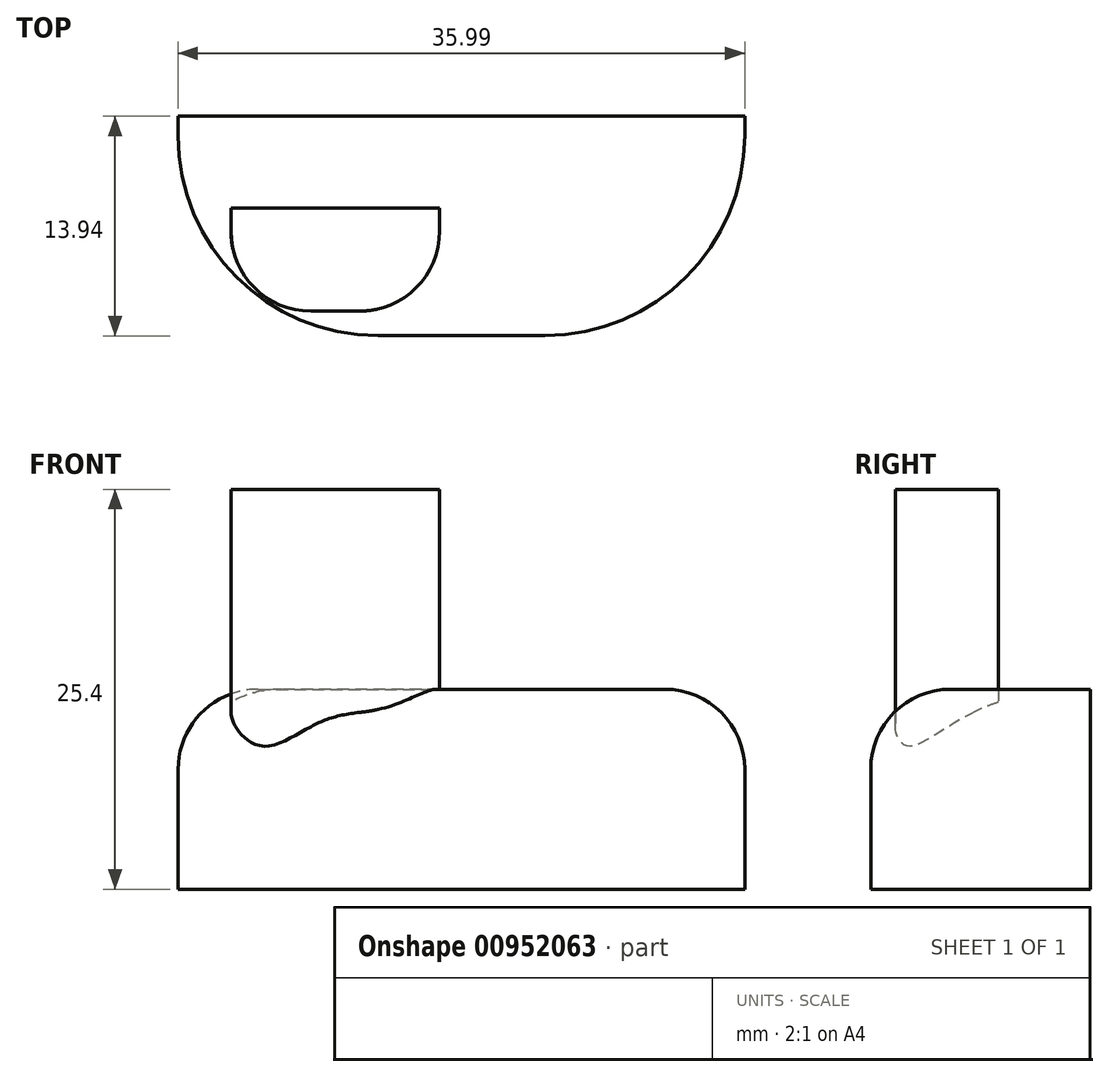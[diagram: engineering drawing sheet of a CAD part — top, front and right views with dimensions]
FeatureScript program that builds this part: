
annotation { "Feature Type Name" : "Feature", "Feature Type Description" : "" }
export const myFeature = defineFeature(function(context is Context, id is Id, definition is map)
    precondition{}
    {
        {
            var Q0;
            Q0=qCreatedBy(makeId("Top.planeOp"),FACE);
            var sketch = newSketch(context, id + "F0", { "sketchPlane" : qUnion([Q0])});
            skLineSegment(sketch, "E0.bottom", {"start": v(-20.3, -6.64) * mm, "end": v(15.68, -6.64) * mm});
            skLineSegment(sketch, "E0.top", {"start": v(-20.3, -20.58) * mm, "end": v(15.68, -20.58) * mm});
            skLineSegment(sketch, "E0.left", {"start": v(-20.3, -6.64) * mm, "end": v(-20.3, -20.58) * mm});
            skLineSegment(sketch, "E0.right", {"start": v(15.68, -6.64) * mm, "end": v(15.68, -20.58) * mm});
            skSolve(sketch);
        }
        {
            var Q0;
            Q0=makeQuery(id+"F0.imprint","IMPRINT",FACE,{"disambiguationData":[TD([[makeQuery(id+"F0.imprint","IMPRINT",EDGE,{"derivedFrom":sQuery(id+"F0.wireOp",EDGE,"E0.bottom")}),-1.0]])]});
            extrude(context, id + "F1", {"entities" : qUnion([Q0]), "depth" : 12.7 * mm, "offsetDistance" : 25.4 * mm});
        }
        {
            var Q0;
            Q0=makeQuery(id+"F1.opExtrude","SWEPT_EDGE",EDGE,{"disambiguationData":[OSD([sQuery(id+"F0.wireOp",EDGE,"E0.top"),sQuery(id+"F0.wireOp",EDGE,"E0.right")])]});
            var Q1;
            Q1=makeQuery(id+"F1.opExtrude","SWEPT_EDGE",EDGE,{"disambiguationData":[OSD([sQuery(id+"F0.wireOp",EDGE,"E0.top"),sQuery(id+"F0.wireOp",EDGE,"E0.left")])]});
            fillet(context, id + "F2", {"entities" : qUnion([Q0, Q1]), "radius" : 12.7 * mm, "tangentPropagation" : true, "allowEdgeOverflow" : false});
        }
        {
            var Q0;
            Q0=makeQuery(id+"F1.opExtrude","CAP_FACE",FACE,{"disambiguationData":[OSD([sQuery(id+"F0.wireOp",EDGE,"E0.bottom"),sQuery(id+"F0.wireOp",EDGE,"E0.top"),sQuery(id+"F0.wireOp",EDGE,"E0.left"),sQuery(id+"F0.wireOp",EDGE,"E0.right")])],"isStart":false});
            var sketch = newSketch(context, id + "F3", { "sketchPlane" : qUnion([Q0])});
            skLineSegment(sketch, "E1.bottom", {"start": v(-3.7, -19.01) * mm, "end": v(-16.95, -19.01) * mm});
            skLineSegment(sketch, "E1.top", {"start": v(-3.7, -12.46) * mm, "end": v(-16.95, -12.46) * mm});
            skLineSegment(sketch, "E1.left", {"start": v(-3.7, -19.01) * mm, "end": v(-3.7, -12.46) * mm});
            skLineSegment(sketch, "E1.right", {"start": v(-16.95, -19.01) * mm, "end": v(-16.95, -12.46) * mm});
            skSolve(sketch);
        }
        {
            var Q0;
            {var subQ1=sQuery(id+"F3.wireOp",EDGE,"E1.top");Q0=makeQuery(id+"F3.imprint","IMPRINT",FACE,{"disambiguationData":[TD([[makeQuery(id+"F3.imprint","IMPRINT",EDGE,{"derivedFrom":subQ1}),1.0]])]});}
            var Q1;
            {var subQ0=sQuery(id+"F3.wireOp",EDGE,"E1.right");var subQ1=sQuery(id+"F3.wireOp",EDGE,"E1.bottom");var subQ2=makeQuery(id+"F3.imprint","INTERSECT",VERTEX,{"derivedFrom":[subQ1,subQ0]});Q1=makeQuery(id+"F3.imprint","IMPRINT",FACE,{"disambiguationData":[TD([[makeQuery(id+"F3.imprint","IMPRINT",EDGE,{"disambiguationData":[TD([[subQ2,1.0]])],"derivedFrom":subQ1}),-1.0]])]});}
            extrude(context, id + "F4", {"entities" : qUnion([Q0, Q1]), "operationType" : NewBodyOperationType.ADD, "depth" : 12.7 * mm, "offsetDistance" : 25.4 * mm});
        }
        {
            var Q0;
            Q0=makeQuery(id+"F4.opExtrude","SWEPT_EDGE",EDGE,{"disambiguationData":[OSD([sQuery(id+"F3.wireOp",EDGE,"E1.bottom"),sQuery(id+"F3.wireOp",EDGE,"E1.right")])]});
            var Q1;
            Q1=makeQuery(id+"F4.opExtrude","SWEPT_EDGE",EDGE,{"disambiguationData":[OSD([sQuery(id+"F3.wireOp",EDGE,"E1.bottom"),sQuery(id+"F3.wireOp",EDGE,"E1.left")])]});
            fillet(context, id + "F5", {"entities" : qUnion([Q0, Q1]), "radius" : 5.08 * mm, "tangentPropagation" : true, "allowEdgeOverflow" : false});
        }
        {
            var Q0;
            {var subQ3=sQuery(id+"F0.wireOp",EDGE,"E0.left");var subQ4=sQuery(id+"F0.wireOp",EDGE,"E0.top");var subQ5=makeQuery(id+"F2.opFillet","BLEND_FACE",FACE,{"disambiguationData":[OSD([subQ4,subQ3])]});var subQ6=makeQuery(id+"F1.opExtrude","CAP_FACE",FACE,{"disambiguationData":[OSD([sQuery(id+"F0.wireOp",EDGE,"E0.bottom"),subQ4,subQ3,sQuery(id+"F0.wireOp",EDGE,"E0.right")])],"isStart":false});var subQ7=makeQuery(id+"F2.opFillet","BLEND_EDGE",EDGE,{"blendedFrom":[makeQuery(id+"F1.opExtrude","SWEPT_EDGE",EDGE,{"disambiguationData":[OSD([subQ4,subQ3])]}),subQ6],"blendedInto":[subQ6]});Q0=makeQuery(id+"F5.opFillet","MERGE",EDGE,{"derivedFrom":[makeQuery(id+"F4.boolean.opBoolean","SPLIT",EDGE,{"disambiguationData":[topologyDisambiguationEdgeConnected([subQ6,subQ5]),TD([makeQuery(id+"F1.opExtrude","SWEPT_FACE",FACE,{"disambiguationData":[OSD([subQ4])]})])],"derivedFrom":subQ7}),makeQuery(id+"F4.boolean.opBoolean","SPLIT",EDGE,{"disambiguationData":[topologyDisambiguationEdgeConnected([subQ6,subQ5]),TD([makeQuery(id+"F1.opExtrude","SWEPT_FACE",FACE,{"disambiguationData":[OSD([subQ3])]})])],"derivedFrom":subQ7})]});}
            fillet(context, id + "F6", {"entities" : qUnion([Q0]), "radius" : 5.08 * mm, "tangentPropagation" : true, "allowEdgeOverflow" : false});
        }
    });
